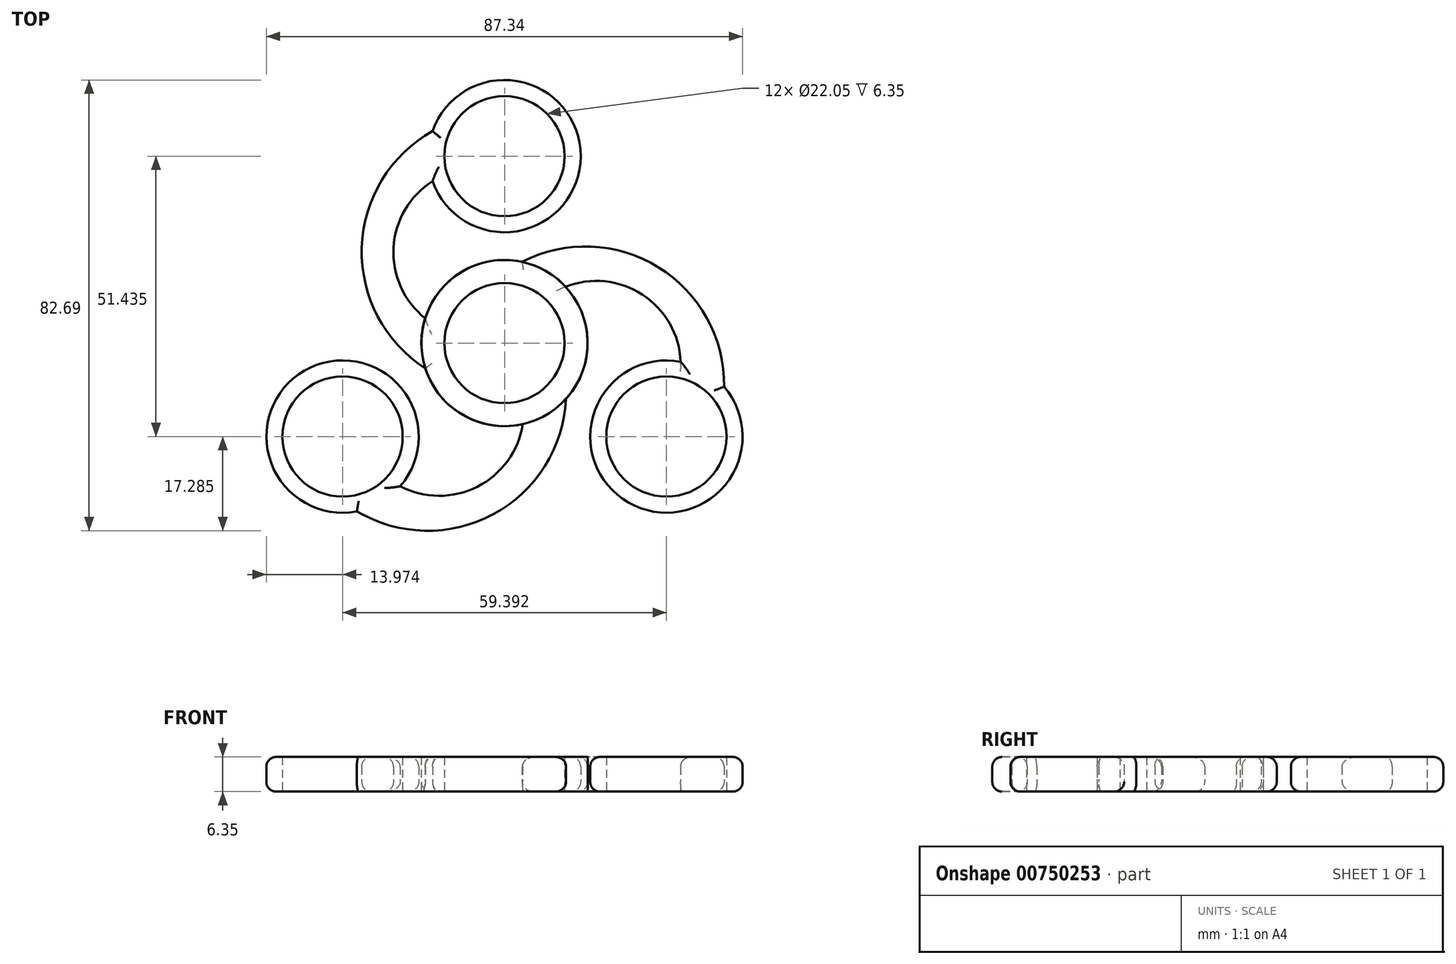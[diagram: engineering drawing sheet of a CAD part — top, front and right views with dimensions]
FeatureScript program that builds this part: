
annotation { "Feature Type Name" : "Feature", "Feature Type Description" : "" }
export const myFeature = defineFeature(function(context is Context, id is Id, definition is map)
    precondition{}
    {
        {
            var Q0;
            Q0=qCreatedBy(makeId("Top.planeOp"),FACE);
            var sketch = newSketch(context, id + "F0", { "sketchPlane" : qUnion([Q0])});
            skCircle(sketch, "E0", {"center": v(0, 0) * mm, "radius": 15.24 * mm});
            skCircle(sketch, "E1", {"center": v(0, 0) * mm, "radius": 11.02 * mm});
            skCircle(sketch, "E2", {"center": v(0, 34.3) * mm, "radius": 11.02 * mm});
            skCircle(sketch, "E3", {"center": v(0, 34.3) * mm, "radius": 13.97 * mm});
            skLineSegment(sketch, "E4", {"start": v(0, 34.3) * mm, "end": v(-13.97, 34.3) * mm});
            skLineSegment(sketch, "E5", {"start": v(0, 34.3) * mm, "end": v(13.97, 34.3) * mm});
            skLineSegment(sketch, "E6", {"start": v(0, 0) * mm, "end": v(-15.24, 0) * mm});
            skLineSegment(sketch, "E7", {"start": v(0, 0) * mm, "end": v(15.24, 0) * mm});
            skArc(sketch, "E8", {"start": v(-13.2, 29.7) * mm, "mid": v(-20.34, 17.47) * mm, "end": v(-14.55, 4.54) * mm});
            skArc(sketch, "E9", {"start": v(-13.2, 38.88) * mm, "mid": v(-26.17, 17.5) * mm, "end": v(-14.52, -4.64) * mm});
            skSolve(sketch);
        }
        {
            var Q0;
            {var subQ0=sQuery(id+"F0.wireOp",EDGE,"E4");var subQ4=sQuery(id+"F0.wireOp",EDGE,"E2");var subQ5=makeQuery(id+"F0.imprint","INTERSECT",VERTEX,{"derivedFrom":[subQ4,subQ0]});Q0=makeQuery(id+"F0.imprint","IMPRINT",FACE,{"disambiguationData":[TD([[makeQuery(id+"F0.imprint","IMPRINT",EDGE,{"disambiguationData":[TD([[subQ5,1.0]])],"derivedFrom":subQ4}),-1.0]])]});}
            var Q1;
            {var subQ0=sQuery(id+"F0.wireOp",EDGE,"E4");var subQ3=sQuery(id+"F0.wireOp",EDGE,"E2");var subQ4=makeQuery(id+"F0.imprint","INTERSECT",VERTEX,{"derivedFrom":[subQ3,subQ0]});Q1=makeQuery(id+"F0.imprint","IMPRINT",FACE,{"disambiguationData":[TD([[makeQuery(id+"F0.imprint","IMPRINT",EDGE,{"disambiguationData":[TD([[subQ4,-1.0]])],"derivedFrom":subQ3}),-1.0]])]});}
            var Q2;
            {var subQ1=sQuery(id+"F0.wireOp",EDGE,"E0");var subQ5=sQuery(id+"F0.wireOp",EDGE,"E7");var subQ8=makeQuery(id+"F0.imprint","INTERSECT",VERTEX,{"derivedFrom":[subQ1,subQ5]});Q2=makeQuery(id+"F0.imprint","IMPRINT",FACE,{"disambiguationData":[TD([[makeQuery(id+"F0.imprint","IMPRINT",EDGE,{"disambiguationData":[TD([[subQ8,-1.0]])],"derivedFrom":subQ1}),1.0]])]});}
            var Q3;
            {var subQ2=sQuery(id+"F0.wireOp",EDGE,"E8");Q3=makeQuery(id+"F0.imprint","IMPRINT",FACE,{"disambiguationData":[TD([[makeQuery(id+"F0.imprint","IMPRINT",EDGE,{"derivedFrom":subQ2}),-1.0]])]});}
            var Q4;
            {var subQ0=sQuery(id+"F0.wireOp",EDGE,"E6");var subQ5=sQuery(id+"F0.wireOp",EDGE,"E0");var subQ8=makeQuery(id+"F0.imprint","INTERSECT",VERTEX,{"derivedFrom":[subQ5,subQ0]});Q4=makeQuery(id+"F0.imprint","IMPRINT",FACE,{"disambiguationData":[TD([[makeQuery(id+"F0.imprint","IMPRINT",EDGE,{"disambiguationData":[TD([[subQ8,-1.0]])],"derivedFrom":subQ5}),1.0]])]});}
            extrude(context, id + "F1", {"entities" : qUnion([Q0, Q1, Q2, Q3, Q4]), "depth" : 6.35 * mm, "offsetDistance" : 25.4 * mm});
        }
        {
            var Q0;
            Q0=makeQuery(id+"F1.opExtrude","SWEPT_BODY",BODY,{"disambiguationData":[OSD([sQuery(id+"F0.wireOp",EDGE,"E0"),sQuery(id+"F0.wireOp",EDGE,"E1"),sQuery(id+"F0.wireOp",EDGE,"E2"),sQuery(id+"F0.wireOp",EDGE,"E3"),sQuery(id+"F0.wireOp",EDGE,"E8"),sQuery(id+"F0.wireOp",EDGE,"E9")])]});
            var Q1;
            Q1=makeQuery(id+"F1.opExtrude","CAP_EDGE",EDGE,{"disambiguationData":[OSD([sQuery(id+"F0.wireOp",EDGE,"E1")])],"isStart":false});
            circularPattern(context, id + "F2", {"entities" : qUnion([Q0]), "axis" : qUnion([Q1]), "angle" : 360 * degree, "instanceCount" : 3, "equalSpace" : true});
        }
        {
            var Q0;
            Q0=makeQuery(id+"F1.opExtrude","CAP_EDGE",EDGE,{"disambiguationData":[OSD([sQuery(id+"F0.wireOp",EDGE,"E3")])],"isStart":false});
            var Q1;
            Q1=makeQuery(id+"F1.opExtrude","CAP_EDGE",EDGE,{"disambiguationData":[OSD([sQuery(id+"F0.wireOp",EDGE,"E8")])],"isStart":false});
            var Q2;
            Q2=makeQuery(id+"F1.opExtrude","CAP_EDGE",EDGE,{"disambiguationData":[OSD([sQuery(id+"F0.wireOp",EDGE,"E9")])],"isStart":false});
            var Q3;
            Q3=makeQuery(id+"F1.opExtrude","CAP_EDGE",EDGE,{"disambiguationData":[OSD([sQuery(id+"F0.wireOp",EDGE,"E0")])],"isStart":false});
            var Q4;
            Q4=makeQuery(id+"F2.opPattern","COPY",EDGE,{"derivedFrom":makeQuery(id+"F1.opExtrude","CAP_EDGE",EDGE,{"disambiguationData":[OSD([sQuery(id+"F0.wireOp",EDGE,"E9")])],"isStart":false}),"instanceName":"1"});
            var Q5;
            Q5=makeQuery(id+"F2.opPattern","COPY",EDGE,{"derivedFrom":makeQuery(id+"F1.opExtrude","CAP_EDGE",EDGE,{"disambiguationData":[OSD([sQuery(id+"F0.wireOp",EDGE,"E3")])],"isStart":false}),"instanceName":"1"});
            var Q6;
            Q6=makeQuery(id+"F2.opPattern","COPY",EDGE,{"derivedFrom":makeQuery(id+"F1.opExtrude","CAP_EDGE",EDGE,{"disambiguationData":[OSD([sQuery(id+"F0.wireOp",EDGE,"E9")])],"isStart":false}),"instanceName":"2"});
            var Q7;
            Q7=makeQuery(id+"F2.opPattern","COPY",EDGE,{"derivedFrom":makeQuery(id+"F1.opExtrude","CAP_EDGE",EDGE,{"disambiguationData":[OSD([sQuery(id+"F0.wireOp",EDGE,"E8")])],"isStart":false}),"instanceName":"2"});
            var Q8;
            Q8=makeQuery(id+"F2.opPattern","COPY",EDGE,{"derivedFrom":makeQuery(id+"F1.opExtrude","CAP_EDGE",EDGE,{"disambiguationData":[OSD([sQuery(id+"F0.wireOp",EDGE,"E3")])],"isStart":false}),"instanceName":"2"});
            var Q9;
            Q9=makeQuery(id+"F2.opPattern","COPY",EDGE,{"derivedFrom":makeQuery(id+"F1.opExtrude","CAP_EDGE",EDGE,{"disambiguationData":[OSD([sQuery(id+"F0.wireOp",EDGE,"E3")])],"isStart":true}),"instanceName":"1"});
            var Q10;
            Q10=makeQuery(id+"F2.opPattern","COPY",EDGE,{"derivedFrom":makeQuery(id+"F1.opExtrude","CAP_EDGE",EDGE,{"disambiguationData":[OSD([sQuery(id+"F0.wireOp",EDGE,"E9")])],"isStart":true}),"instanceName":"1"});
            var Q11;
            Q11=makeQuery(id+"F2.opPattern","COPY",EDGE,{"derivedFrom":makeQuery(id+"F1.opExtrude","CAP_EDGE",EDGE,{"disambiguationData":[OSD([sQuery(id+"F0.wireOp",EDGE,"E0")])],"isStart":true}),"instanceName":"2"});
            var Q12;
            Q12=makeQuery(id+"F2.opPattern","COPY",EDGE,{"derivedFrom":makeQuery(id+"F1.opExtrude","CAP_EDGE",EDGE,{"disambiguationData":[OSD([sQuery(id+"F0.wireOp",EDGE,"E9")])],"isStart":true}),"instanceName":"2"});
            var Q13;
            Q13=makeQuery(id+"F2.opPattern","COPY",EDGE,{"derivedFrom":makeQuery(id+"F1.opExtrude","CAP_EDGE",EDGE,{"disambiguationData":[OSD([sQuery(id+"F0.wireOp",EDGE,"E3")])],"isStart":true}),"instanceName":"2"});
            var Q14;
            Q14=makeQuery(id+"F1.opExtrude","CAP_EDGE",EDGE,{"disambiguationData":[OSD([sQuery(id+"F0.wireOp",EDGE,"E9")])],"isStart":true});
            var Q15;
            Q15=makeQuery(id+"F1.opExtrude","CAP_EDGE",EDGE,{"disambiguationData":[OSD([sQuery(id+"F0.wireOp",EDGE,"E8")])],"isStart":true});
            var Q16;
            Q16=makeQuery(id+"F1.opExtrude","CAP_EDGE",EDGE,{"disambiguationData":[OSD([sQuery(id+"F0.wireOp",EDGE,"E3")])],"isStart":true});
            var Q17;
            Q17=makeQuery(id+"F2.opPattern","COPY",EDGE,{"derivedFrom":makeQuery(id+"F1.opExtrude","CAP_EDGE",EDGE,{"disambiguationData":[OSD([sQuery(id+"F0.wireOp",EDGE,"E8")])],"isStart":true}),"instanceName":"1"});
            var Q18;
            Q18=makeQuery(id+"F2.opPattern","COPY",EDGE,{"derivedFrom":makeQuery(id+"F1.opExtrude","CAP_EDGE",EDGE,{"disambiguationData":[OSD([sQuery(id+"F0.wireOp",EDGE,"E8")])],"isStart":false}),"instanceName":"1"});
            fillet(context, id + "F3", {"entities" : qUnion([Q0, Q1, Q2, Q3, Q4, Q5, Q6, Q7, Q8, Q9, Q10, Q11, Q12, Q13, Q14, Q15, Q16, Q17, Q18]), "radius" : 1.78 * mm, "tangentPropagation" : true, "allowEdgeOverflow" : false});
        }
    });
